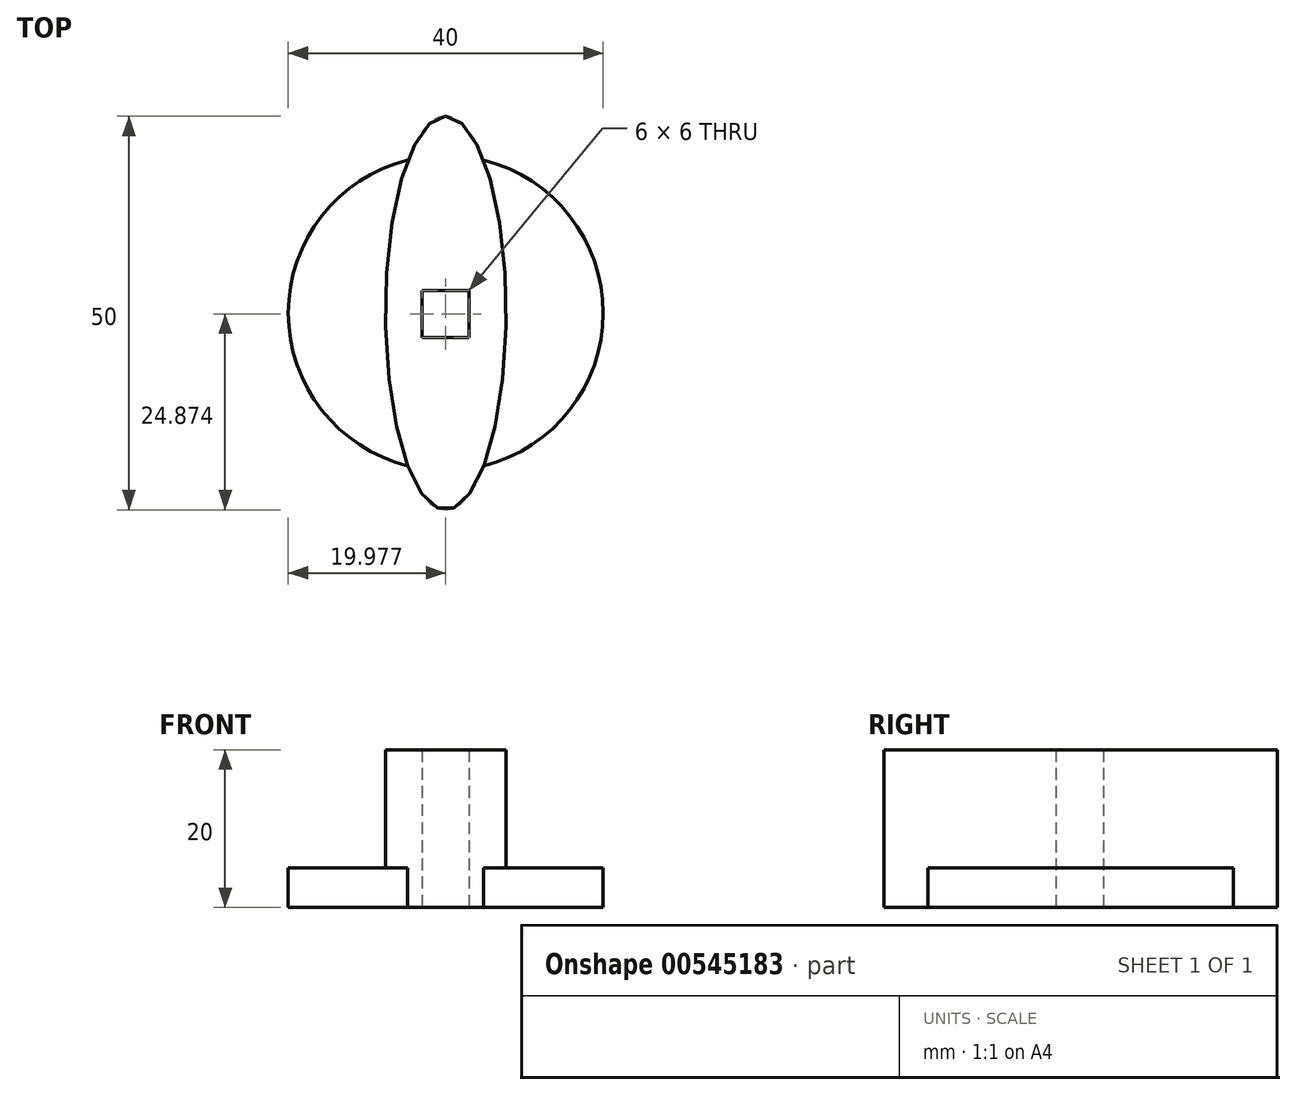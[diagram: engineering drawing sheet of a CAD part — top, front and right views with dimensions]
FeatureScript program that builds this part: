
annotation { "Feature Type Name" : "Feature", "Feature Type Description" : "" }
export const myFeature = defineFeature(function(context is Context, id is Id, definition is map)
    precondition{}
    {
        {
            var Q0;
            Q0=qCreatedBy(makeId("Top.planeOp"),FACE);
            var sketch = newSketch(context, id + "F0", { "sketchPlane" : qUnion([Q0])});
            skArc(sketch, "E0", {"start": v(-4.83, 19.4) * mm, "mid": v(-20, 0) * mm, "end": v(-4.83, -19.4) * mm});
            skEllipse(sketch, "E1", {"center": v(0, 0) * mm, "majorRadius": 25 * mm, "minorRadius": 7.67 * mm, "majorAxis": v(0, 1)});
            skArc(sketch, "E2.trimOffspring", {"start": v(4.83, -19.4) * mm, "mid": v(20, 0) * mm, "end": v(4.83, 19.4) * mm});
            skLineSegment(sketch, "E3.bottom", {"start": v(-3.02, 2.87) * mm, "end": v(2.98, 2.87) * mm});
            skLineSegment(sketch, "E3.top", {"start": v(-3.02, -3.13) * mm, "end": v(2.98, -3.13) * mm});
            skLineSegment(sketch, "E3.left", {"start": v(-3.02, 2.87) * mm, "end": v(-3.02, -3.13) * mm});
            skLineSegment(sketch, "E3.right", {"start": v(2.98, 2.87) * mm, "end": v(2.98, -3.13) * mm});
            skSolve(sketch);
        }
        {
            var Q0;
            Q0=makeQuery(id+"F0.imprint","IMPRINT",FACE,{"disambiguationData":[TD([[makeQuery(id+"F0.imprint","IMPRINT",EDGE,{"derivedFrom":sQuery(id+"F0.wireOp",EDGE,"E3.bottom")}),1.0]])]});
            extrude(context, id + "F1", {"entities" : qUnion([Q0]), "depth" : 20 * mm, "offsetDistance" : 25 * mm});
        }
        {
            var Q0;
            Q0 = qSketchRegion(id + "F0", true);
            extrude(context, id + "F2", {"entities" : qUnion([Q0]), "operationType" : NewBodyOperationType.ADD, "depth" : 5 * mm, "offsetDistance" : 25 * mm});
        }
    });
